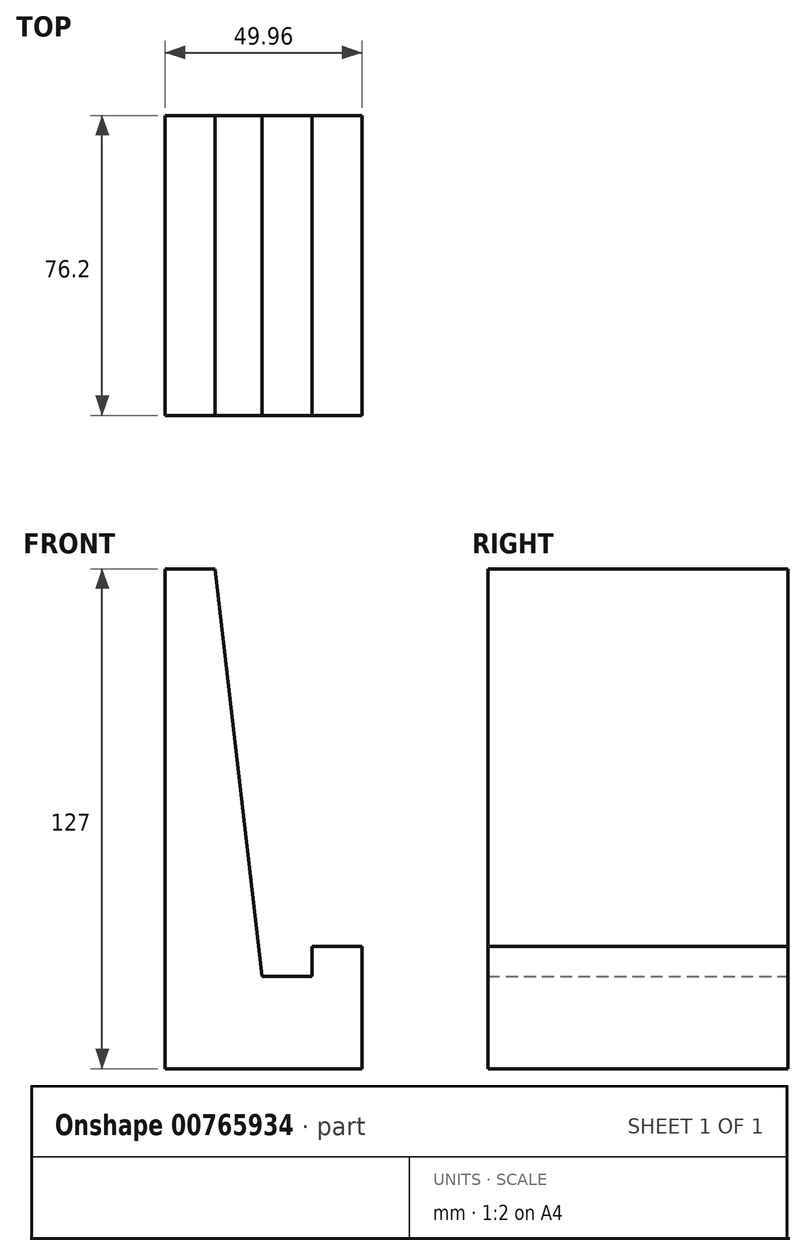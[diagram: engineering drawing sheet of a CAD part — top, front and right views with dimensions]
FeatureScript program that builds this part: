
annotation { "Feature Type Name" : "Feature", "Feature Type Description" : "" }
export const myFeature = defineFeature(function(context is Context, id is Id, definition is map)
    precondition{}
    {
        {
            var Q0;
            Q0=qCreatedBy(makeId("Front.planeOp"),FACE);
            var sketch = newSketch(context, id + "F0", { "sketchPlane" : qUnion([Q0])});
            skLineSegment(sketch, "E0", {"start": v(-60.94, 62.44) * mm, "end": v(-60.94, -64.56) * mm});
            skLineSegment(sketch, "E1", {"start": v(-60.94, 62.44) * mm, "end": v(-48.24, 62.44) * mm});
            skLineSegment(sketch, "E2", {"start": v(-48.24, 62.44) * mm, "end": v(-36.38, -41.15) * mm});
            skLineSegment(sketch, "E3", {"start": v(-36.38, -41.15) * mm, "end": v(-23.68, -41.15) * mm});
            skLineSegment(sketch, "E4", {"start": v(-23.68, -41.15) * mm, "end": v(-23.68, -33.53) * mm});
            skLineSegment(sketch, "E5", {"start": v(-23.68, -33.53) * mm, "end": v(-10.98, -33.53) * mm});
            skLineSegment(sketch, "E6", {"start": v(-10.98, -33.53) * mm, "end": v(-10.98, -64.56) * mm});
            skLineSegment(sketch, "E7", {"start": v(-10.98, -64.56) * mm, "end": v(-60.94, -64.56) * mm});
            skSolve(sketch);
        }
        {
            var Q0;
            Q0=qSketchRegion(id+"F0",true);
            extrude(context, id + "F1", {"entities" : qUnion([Q0]), "depth" : 76.2 * mm, "offsetDistance" : 25.4 * mm});
        }
    });
